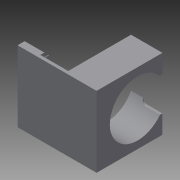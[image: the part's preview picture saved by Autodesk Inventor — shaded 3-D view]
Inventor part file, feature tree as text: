
AUTODESK INVENTOR PART (.ipt)
format: ipt  version: 2015 SP2 (Build 190223200, 223)  size: 173,568 bytes
history: native  units: mm
features: sketch x16, extrude x8, hole x2
ambient origin geometry x8: Origin, YZ Plane, XZ Plane, XY Plane, X Axis, Y Axis, Z Axis, Center Point
bodies: Solid1 (feature_tree)
feature tree (26):
  extrude  "Extrusion1"  Depth=31.0mm
  sketch  "Sketch2"  dims[d2=60.0mm d3=0.0mm d5=55.0mm]
  hole  "Hole1"  [1 undecoded]
  sketch  "Sketch4"  dims[d42=8.0mm d43=8.0mm]
  sketch  "Sketch5"  dims[d44=4.0mm d45=0.0mm d46=4.0mm d47=0.0mm]
  sketch  "Sketch7"  dims[d48=5.0mm d49=6.0mm d50=4.0mm d51=2.0mm d52=90.0deg d53=14.0mm d54=0.0mm d57=47.0mm]
  sketch  "Sketch8"  dims[d63=2.0mm d64=0.0mm d67=5.0mm d68=0.0mm]
  sketch  "Sketch9"  dims[d98=21.0mm d99=0.0mm d120=23.0mm]
  sketch  "Sketch14"  dims[d121=21.0mm d138=4.0mm d139=0.0mm]
  extrude  "Extrusion4"  Depth=4.0mm
  extrude  "Extrusion5"  Depth=8.0mm
  hole  "Hole5"  [1 undecoded]
  sketch  "Sketch18"  dims[d124=1.0mm]
  extrude  "Extrusion9"  Depth=47.0mm
  extrude  "Extrusion11"  Depth=5.0mm TaperAngle=0.0deg
  sketch  "Sketch29"
  extrude  "Extrusion20"  Depth=23.0mm
  sketch  "Sketch37"
  sketch  "Sketch39"
  extrude  "Extrusion25"  Depth=4.0mm TaperAngle=0.0deg
  extrude  "Extrusion26"  Depth=4.0mm TaperAngle=0.0deg
  sketch  "Sketch1"  dims[d0=70.0mm d1=31.0mm]
  sketch  "Sketch3"  dims[d6=55.0mm d7=6.0mm d8=4.0mm d9=2.0mm d10=90.0deg d11=8.0mm d12=20.594885mm d33=4.0mm]
  sketch  "Sketch15"  dims[d140=4.0mm d141=4.0mm d142=0.0mm]
  sketch  "Sketch25"  dims[d125=1.0mm]
  sketch  "Sketch35"
note: 2 required parameter values undecoded (feature->parameter linkage not recoverable at this tier; creation-order binding heuristic only, values carry confidence <= 0.55)
